# Revit family: Mail_Package_Drop-Salsbury_Industries-USPS_Approved
name_source: partatom
category: Specialty Equipment
revit_build: Autodesk Revit 2016 (Build: 20150714_1515(x64)
units: mm (PartAtom-declared; Revit-internal decimal feet)

## family parameters
Always vertical = Yes
Cut with Voids When Loaded = No
OmniClass Number = 23.40.90.14.11
OmniClass Title = Mail Boxes
Part Type = Normal
Room Calculation Point = No
Round Connector Dimension = Use Diameter
Shared = No
Work Plane-Based = No

## types (2) — shared parameters
Assembly Code = C1030910
Assembly Description = Mailboxes
Depth = 23 "
Description = Manufactured to USPS-STD-7B specifications; package drop opening; two user access locking compartments
Flag Powder Coated Finish = Paint - Salsbury Finish - Red
Flag Vertical Position = 41.937 "
Hardware Material = Stainless Steel - Salsbury Finish -  Polished
Height = 36 "
Manufacturer = Salsbury Industries
MasterFormat Number = 10 55 00
MasterFormat Title = Postal Specialties
Model = 4375
OmniClass 23 Number = 23.40.90.14.11
OmniClass 23 Title = Mail Boxes
Pedestal Height = 16 "
Type Comments = Mail Drop - U.S.P.S. Approved (Pedestal not included, order separately)
URL = www.mailboxes.com
Version = 1.0 (07/31/19)
Width = 14.375 "

## type names (no varying parameters)
- 4375 (with 4395 pedestal)
- 4375 (with 4385 pedestal)

## geometry (parser evidence)
native form markers: Sweep x6
no freeform markers — native parametric forms only
